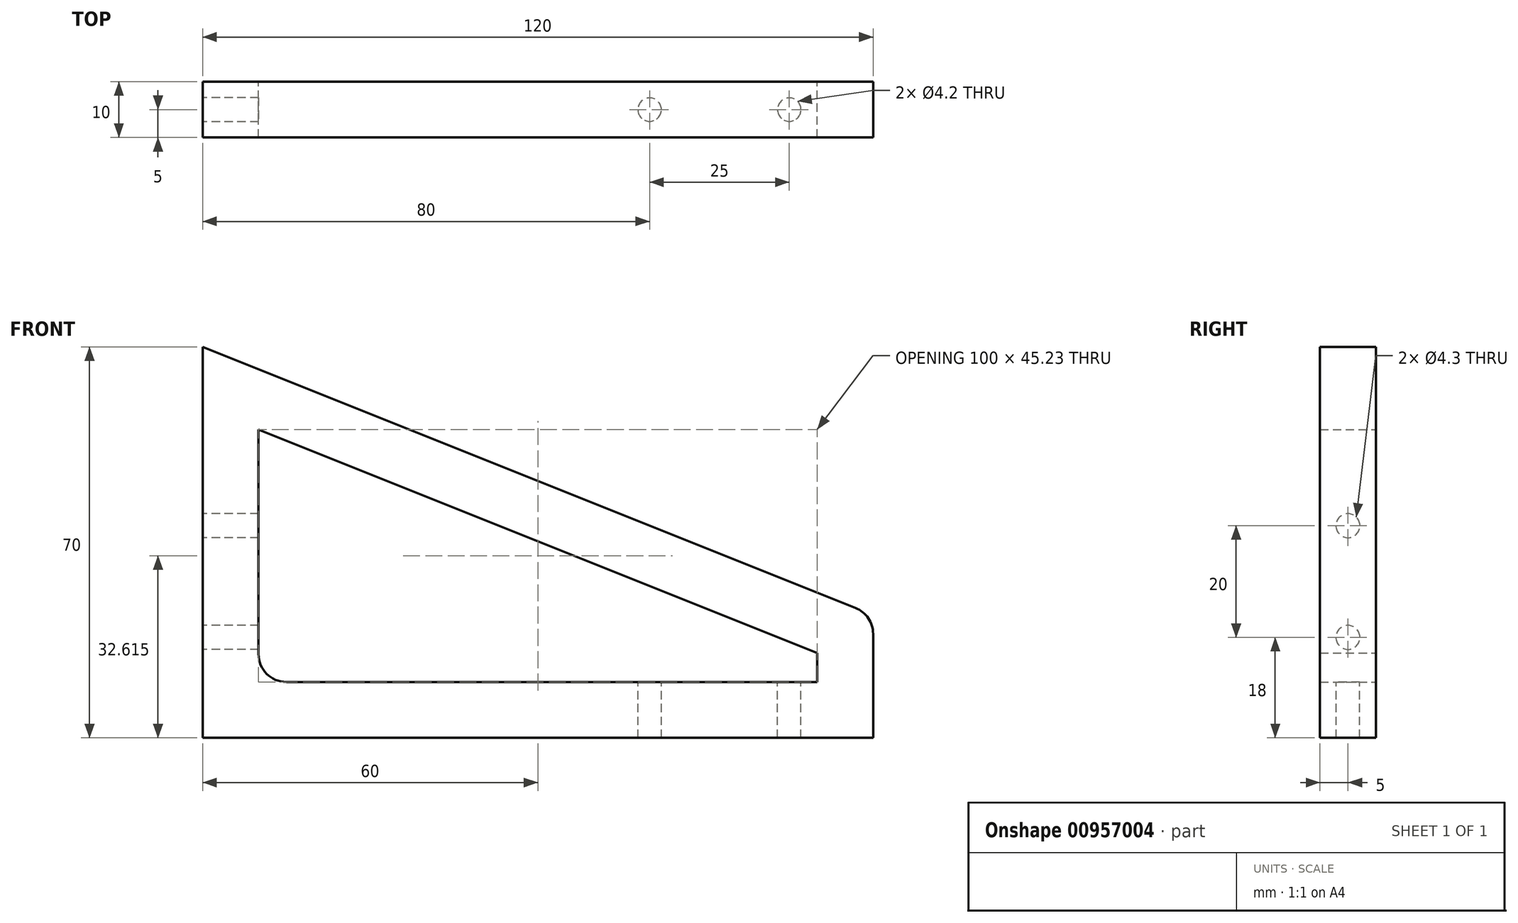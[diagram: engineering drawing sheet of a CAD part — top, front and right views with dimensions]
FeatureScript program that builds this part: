
annotation { "Feature Type Name" : "Feature", "Feature Type Description" : "" }
export const myFeature = defineFeature(function(context is Context, id is Id, definition is map)
    precondition{}
    {
        {
            var Q0;
            Q0=qCreatedBy(makeId("Front.planeOp"),FACE);
            var sketch = newSketch(context, id + "F0", { "sketchPlane" : qUnion([Q0])});
            skLineSegment(sketch, "E0", {"start": v(0, 0) * mm, "end": v(0, 70) * mm});
            skLineSegment(sketch, "E1", {"start": v(0, 70) * mm, "end": v(120, 22) * mm});
            skLineSegment(sketch, "E2", {"start": v(120, 22) * mm, "end": v(120, 0) * mm});
            skLineSegment(sketch, "E3", {"start": v(120, 0) * mm, "end": v(0, 0) * mm});
            skSolve(sketch);
        }
        {
            var Q0;
            Q0 = qSketchRegion(id + "F0", true);
            extrude(context, id + "F1", {"entities" : qUnion([Q0]), "depth" : 10 * mm, "offsetDistance" : 25 * mm});
        }
        {
            var Q0;
            Q0=makeQuery(id+"F1.opExtrude","SWEPT_EDGE",EDGE,{"disambiguationData":[OSD([sQuery(id+"F0.wireOp",EDGE,"E1"),sQuery(id+"F0.wireOp",EDGE,"E2")])]});
            fillet(context, id + "F2", {"entities" : qUnion([Q0]), "radius" : 5 * mm, "tangentPropagation" : true, "allowEdgeOverflow" : false});
        }
        {
            var Q0;
            Q0=qCreatedBy(makeId("Front.planeOp"),FACE);
            var sketch = newSketch(context, id + "F3", { "sketchPlane" : qUnion([Q0])});
            skLineSegment(sketch, "E4", {"start": v(10, 10) * mm, "end": v(10, 55.23) * mm});
            skLineSegment(sketch, "E5", {"start": v(110, 15.23) * mm, "end": v(110, 10) * mm});
            skLineSegment(sketch, "E6", {"start": v(10, 10) * mm, "end": v(110, 10) * mm});
            skLineSegment(sketch, "E7", {"start": v(10, 55.23) * mm, "end": v(110, 15.23) * mm});
            skSolve(sketch);
        }
        {
            var Q0;
            Q0 = qSketchRegion(id + "F3", true);
            extrude(context, id + "F4", {"entities" : qUnion([Q0]), "operationType" : NewBodyOperationType.REMOVE, "endBound" : BoundingType.THROUGH_ALL, "depth" : 25 * mm, "offsetDistance" : 25 * mm});
        }
        {
            var Q0;
            Q0=makeQuery(id+"F4.boolean.opBoolean","COPY",EDGE,{"derivedFrom":makeQuery(id+"F4.opExtrude","SWEPT_EDGE",EDGE,{"disambiguationData":[OSD([sQuery(id+"F3.wireOp",EDGE,"E4"),sQuery(id+"F3.wireOp",EDGE,"E6")])]})});
            fillet(context, id + "F5", {"entities" : qUnion([Q0]), "radius" : 5 * mm, "tangentPropagation" : true, "allowEdgeOverflow" : false});
        }
        {
            var Q0;
            Q0=makeQuery(id+"F4.boolean.opBoolean","COPY",FACE,{"derivedFrom":makeQuery(id+"F4.opExtrude","SWEPT_FACE",FACE,{"disambiguationData":[OSD([sQuery(id+"F3.wireOp",EDGE,"E6")])]})});
            var sketch = newSketch(context, id + "F6", { "sketchPlane" : qUnion([Q0])});
            skPoint(sketch, "E8", {"position": v(105, -5) * mm});
            skPoint(sketch, "E9", {"position": v(80, -5) * mm});
            skSolve(sketch);
        }
        {
            var Q0;
            Q0=sQuery(id+"F6.wireOp",VERTEX,"E9");
            var Q1;
            Q1=sQuery(id+"F6.wireOp",VERTEX,"E8");
            var Q2;
            Q2=makeQuery(id+"F1.opExtrude","SWEPT_BODY",BODY,{"disambiguationData":[OSD([sQuery(id+"F0.wireOp",EDGE,"E0"),sQuery(id+"F0.wireOp",EDGE,"E1"),sQuery(id+"F0.wireOp",EDGE,"E2"),sQuery(id+"F0.wireOp",EDGE,"E3")])]});
            hole(context, id + "F7", {"style" : HoleStyle.SIMPLE, "endStyle" : HoleEndStyle.THROUGH, "standardTappedOrClearance" : lookupTablePath({ "standard" : "ISO", "size" : "4.2", "type" : "Drilled" }), "standardBlindInLast" : lookupTablePath({ "standard" : "ISO", "size" : "4.2", "type" : "Drilled" }), "holeDiameter" : 4.2 * mm, "majorDiameter" : 5 * mm, "isTappedThrough" : true, "tappedDepth" : 12 * mm, "tapClearance" : 3, "locations" : qUnion([Q0, Q1]), "scope" : qUnion([Q2])});
        }
        {
            var Q0;
            Q0=qCreatedBy(makeId("Right.planeOp"),FACE);
            var sketch = newSketch(context, id + "F8", { "sketchPlane" : qUnion([Q0])});
            skPoint(sketch, "E10", {"position": v(-5, 18) * mm});
            skPoint(sketch, "E11", {"position": v(-5, 38) * mm});
            skSolve(sketch);
        }
        {
            var Q0;
            Q0=sQuery(id+"F8.wireOp",VERTEX,"E11");
            var Q1;
            Q1=sQuery(id+"F8.wireOp",VERTEX,"E10");
            var Q2;
            Q2=makeQuery(id+"F1.opExtrude","SWEPT_BODY",BODY,{"disambiguationData":[OSD([sQuery(id+"F0.wireOp",EDGE,"E0"),sQuery(id+"F0.wireOp",EDGE,"E1"),sQuery(id+"F0.wireOp",EDGE,"E2"),sQuery(id+"F0.wireOp",EDGE,"E3")])]});
            hole(context, id + "F9", {"style" : HoleStyle.SIMPLE, "endStyle" : HoleEndStyle.BLIND, "oppositeDirection" : true, "standardTappedOrClearance" : lookupTablePath({ "standard" : "ISO", "size" : "4.3", "type" : "Drilled" }), "standardBlindInLast" : lookupTablePath({ "standard" : "ISO", "size" : "4.3", "type" : "Drilled" }), "holeDiameter" : 4.3 * mm, "majorDiameter" : 5 * mm, "holeDepth" : 15 * mm, "isTappedThrough" : true, "tappedDepth" : 12 * mm, "tapClearance" : 3, "locations" : qUnion([Q0, Q1]), "scope" : qUnion([Q2])});
        }
    });
